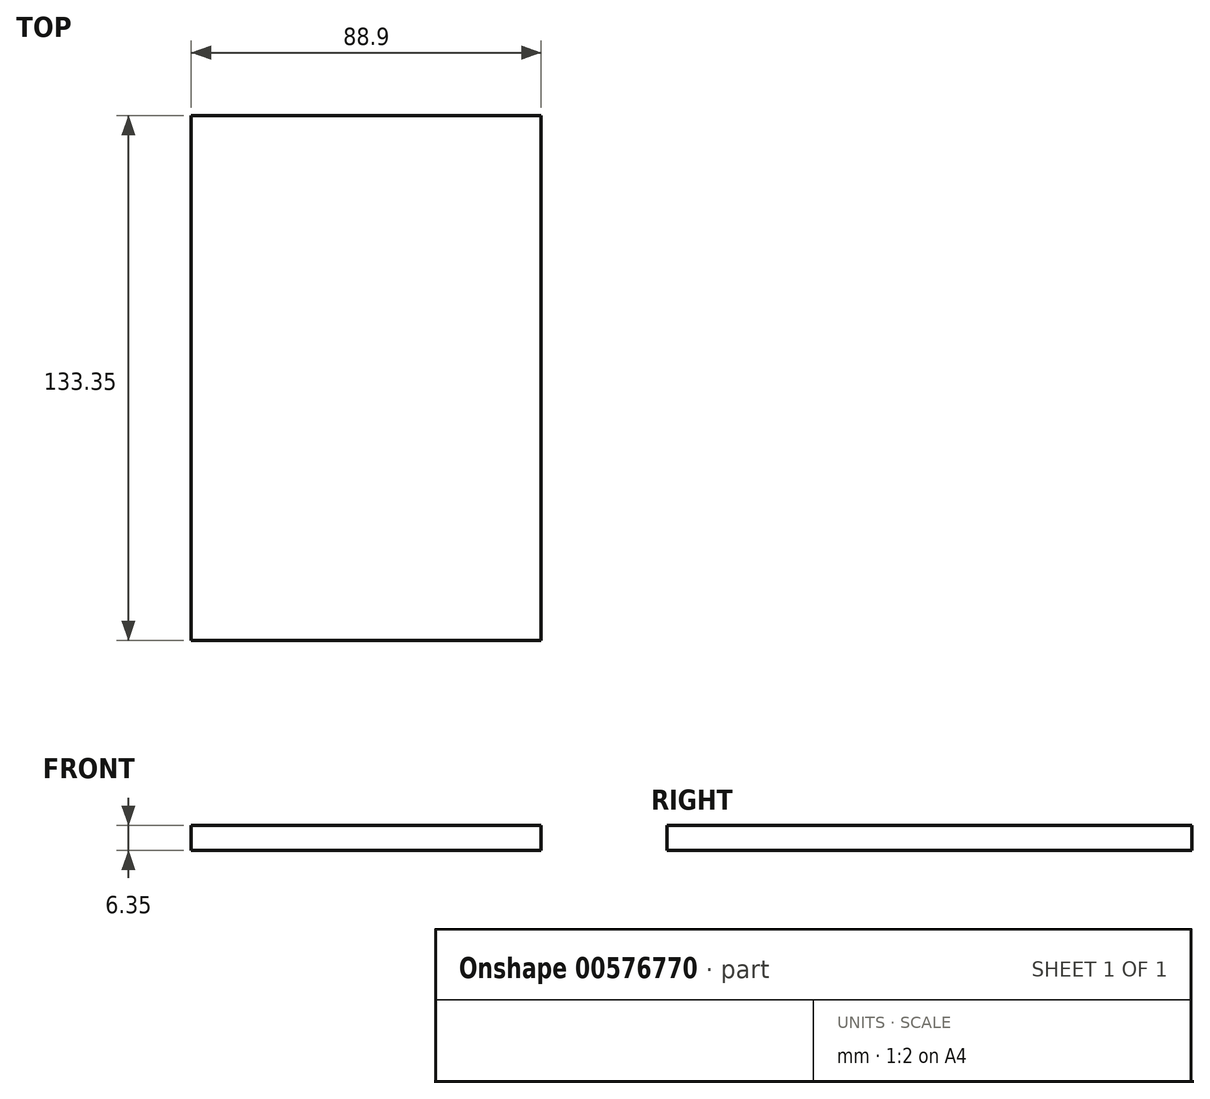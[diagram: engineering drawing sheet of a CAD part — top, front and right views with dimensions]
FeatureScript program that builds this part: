
annotation { "Feature Type Name" : "Feature", "Feature Type Description" : "" }
export const myFeature = defineFeature(function(context is Context, id is Id, definition is map)
    precondition{}
    {
        {
            var Q0;
            Q0=qCreatedBy(makeId("Top.planeOp"),FACE);
            var sketch = newSketch(context, id + "F0", { "sketchPlane" : qUnion([Q0])});
            skLineSegment(sketch, "E0.bottom", {"start": v(-37.01, 63.95) * mm, "end": v(51.89, 63.95) * mm});
            skLineSegment(sketch, "E0.top", {"start": v(-37.01, -69.4) * mm, "end": v(51.89, -69.4) * mm});
            skLineSegment(sketch, "E0.left", {"start": v(-37.01, 63.95) * mm, "end": v(-37.01, -69.4) * mm});
            skLineSegment(sketch, "E0.right", {"start": v(51.89, 63.95) * mm, "end": v(51.89, -69.4) * mm});
            skSolve(sketch);
        }
        {
            var Q0;
            Q0 = qSketchRegion(id + "F0", true);
            extrude(context, id + "F1", {"entities" : qUnion([Q0]), "depth" : 6.35 * mm, "offsetDistance" : 25.4 * mm});
        }
    });
